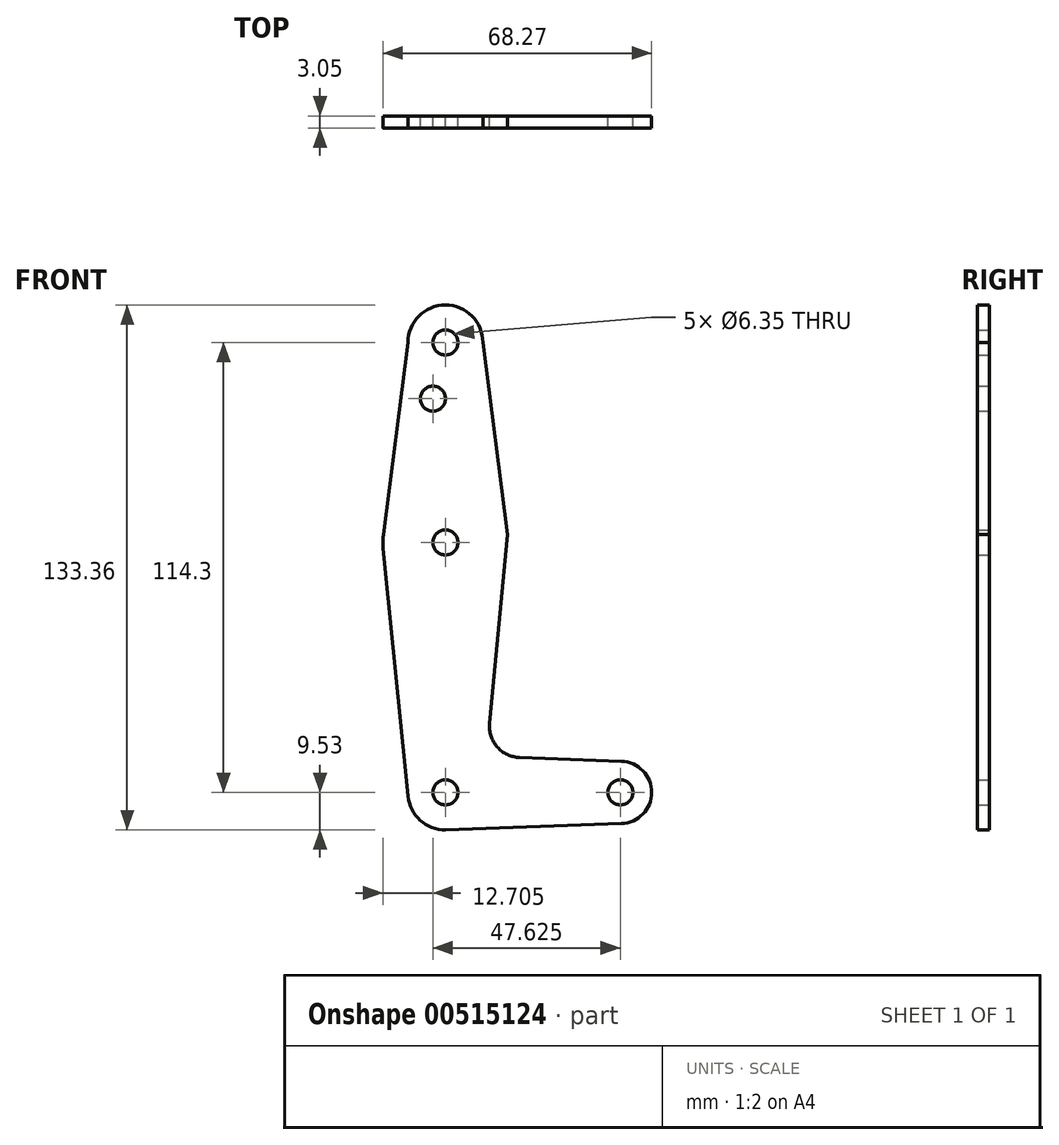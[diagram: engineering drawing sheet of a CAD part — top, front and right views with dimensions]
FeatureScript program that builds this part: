
annotation { "Feature Type Name" : "Feature", "Feature Type Description" : "" }
export const myFeature = defineFeature(function(context is Context, id is Id, definition is map)
    precondition{}
    {
        {
            var Q0;
            Q0=qCreatedBy(makeId("Front.planeOp"),FACE);
            var sketch = newSketch(context, id + "F0", { "sketchPlane" : qUnion([Q0])});
            skLineSegment(sketch, "E0", {"start": v(0, 0) * mm, "end": v(0, 63.5) * mm});
            skLineSegment(sketch, "E1", {"start": v(0, 0) * mm, "end": v(0, 114.3) * mm, "construction": true});
            skLineSegment(sketch, "E2", {"start": v(0, 0) * mm, "end": v(44.45, 0) * mm, "construction": true});
            skCircle(sketch, "E3", {"center": v(44.45, 0) * mm, "radius": 7.94 * mm});
            skCircle(sketch, "E4", {"center": v(0, 63.5) * mm, "radius": 15.88 * mm});
            skCircle(sketch, "E5", {"center": v(0, 114.3) * mm, "radius": 9.53 * mm});
            skCircle(sketch, "E6", {"center": v(0, 0) * mm, "radius": 9.53 * mm});
            skLineSegment(sketch, "E7", {"start": v(9.53, 114.3) * mm, "end": v(15.75, 65.5) * mm});
            skLineSegment(sketch, "E8", {"start": v(-9.53, 114.3) * mm, "end": v(-15.75, 65.5) * mm});
            skLineSegment(sketch, "E9", {"start": v(15.75, 65.5) * mm, "end": v(11.22, 17.55) * mm});
            skLineSegment(sketch, "E10", {"start": v(0, -9.53) * mm, "end": v(44.73, -7.93) * mm});
            skLineSegment(sketch, "E11", {"start": v(18.85, 8.85) * mm, "end": v(44.73, 7.93) * mm});
            skCircle(sketch, "E12", {"center": v(0, 114.3) * mm, "radius": 3.18 * mm});
            skCircle(sketch, "E13", {"center": v(0, 63.5) * mm, "radius": 3.18 * mm});
            skCircle(sketch, "E14", {"center": v(0, 0) * mm, "radius": 3.18 * mm});
            skCircle(sketch, "E15", {"center": v(44.45, 0) * mm, "radius": 3.18 * mm});
            skCircle(sketch, "E16", {"center": v(-3.18, 100.03) * mm, "radius": 3.18 * mm});
            skPoint(sketch, "E17.newPointA", {"position": v(0, 9.53) * mm});
            skArc(sketch, "E17.filletArc", {"start": v(11.22, 17.55) * mm, "mid": v(13.16, 11.55) * mm, "end": v(18.85, 8.85) * mm});
            skLineSegment(sketch, "E18", {"start": v(-15.8, 61.95) * mm, "end": v(-9.48, -0.95) * mm});
            skSolve(sketch);
        }
        {
            var Q0;
            Q0=makeQuery(id+"F0.imprint","IMPRINT",FACE,{"disambiguationData":[TD([[makeQuery(id+"F0.imprint","IMPRINT",EDGE,{"derivedFrom":sQuery(id+"F0.wireOp",EDGE,"E12")}),-1.0]])]});
            var Q1;
            {var subQ1=sQuery(id+"F0.wireOp",EDGE,"E7");Q1=makeQuery(id+"F0.imprint","IMPRINT",FACE,{"disambiguationData":[TD([[makeQuery(id+"F0.imprint","IMPRINT",EDGE,{"derivedFrom":subQ1}),-1.0]])]});}
            var Q2;
            Q2=makeQuery(id+"F0.imprint","IMPRINT",FACE,{"disambiguationData":[TD([[makeQuery(id+"F0.imprint","IMPRINT",EDGE,{"derivedFrom":sQuery(id+"F0.wireOp",EDGE,"E13")}),-1.0]])]});
            var Q3;
            {var subQ12=sQuery(id+"F0.wireOp",EDGE,"E11");Q3=makeQuery(id+"F0.imprint","IMPRINT",FACE,{"disambiguationData":[TD([[makeQuery(id+"F0.imprint","IMPRINT",EDGE,{"derivedFrom":subQ12}),-1.0]])]});}
            var Q4;
            {var subQ5=sQuery(id+"F0.wireOp",EDGE,"E18");Q4=makeQuery(id+"F0.imprint","IMPRINT",FACE,{"disambiguationData":[TD([[makeQuery(id+"F0.imprint","IMPRINT",EDGE,{"derivedFrom":subQ5}),1.0]])]});}
            var Q5;
            Q5=makeQuery(id+"F0.imprint","IMPRINT",FACE,{"disambiguationData":[TD([[makeQuery(id+"F0.imprint","IMPRINT",EDGE,{"derivedFrom":sQuery(id+"F0.wireOp",EDGE,"E14")}),-1.0]])]});
            var Q6;
            Q6=makeQuery(id+"F0.imprint","IMPRINT",FACE,{"disambiguationData":[TD([[makeQuery(id+"F0.imprint","IMPRINT",EDGE,{"derivedFrom":sQuery(id+"F0.wireOp",EDGE,"E15")}),-1.0]])]});
            extrude(context, id + "F1", {"entities" : qUnion([Q0, Q1, Q2, Q3, Q4, Q5, Q6]), "depth" : 3.05 * mm, "offsetDistance" : 25.4 * mm});
        }
    });
